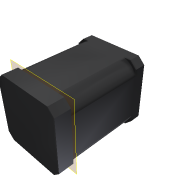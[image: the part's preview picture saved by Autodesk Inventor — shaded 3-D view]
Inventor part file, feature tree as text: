
AUTODESK INVENTOR PART (.ipt)
format: ipt  version: 2014 (Build 180170000, 170)  size: 142,848 bytes
history: native  units: mm
features: extrude x5, sketch x5, chamfer x1, plane x1, pattern_circular x1, projected_geometry x1
ambient origin geometry x8: Origin, YZ Plane, XZ Plane, XY Plane, X Axis, Y Axis, Z Axis, Center Point
bodies: Solid1 (feature_tree)
feature tree (14):
  extrude  "Extrusion1"  Depth=42.0mm
  extrude  "Extrusion2"  Depth=60.0mm
  extrude  "Extrusion3"  Depth=2.0mm
  chamfer  "Chamfer1"  Distance=3.0mm
  extrude  "Extrusion4"  Depth=44.0mm
  plane  "Work Plane1"
  extrude  "Extrusion5"  Depth=44.0mm
  pattern_circular  "Circular Pattern1"  [2 undecoded]
  sketch  "Sketch1"  dims[d0=42.0mm d1=42.0mm]
  sketch  "Sketch3"  dims[d2=60.0mm d3=0.0mm d4=20.0mm]
  sketch  "Sketch4"  dims[d5=2.0mm d6=0.0mm d7=31.0mm]
  sketch  "Sketch5"  dims[d8=31.0mm]
  sketch  "Sketch6"  dims[d9=3.0mm d10=3.0mm d11=3.0mm d12=3.0mm d13=10.0mm d14=0.0mm d15=4.0mm d16=2.0mm d17=45.0deg d18=5.0mm d19=21.0mm d20=0.0mm d21=-9.2mm d22=44.0mm d23=0.0mm d24=40.0mm d25=360.0deg]
  projected_geometry  "Projected Loop1"
note: 2 required parameter values undecoded (feature->parameter linkage not recoverable at this tier; creation-order binding heuristic only, values carry confidence <= 0.55)
